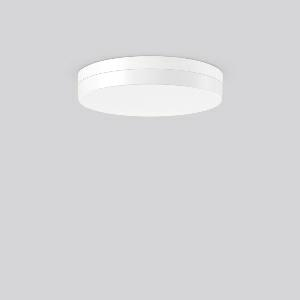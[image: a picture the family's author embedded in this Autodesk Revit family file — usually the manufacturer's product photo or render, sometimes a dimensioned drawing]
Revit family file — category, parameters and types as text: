
# Revit family: flat_slim_round_312631_002_19_3b17
name_source: partatom
category: Lighting Fixtures
units: mm (PartAtom-declared; Revit-internal decimal feet)

## family parameters
Cut with Voids When Loaded = No
Host = Face
Light Source = No
Part Type = Normal
Room Calculation Point = No
Round Connector Dimension = Use Diameter
Shared = No

## types (1)
- MultiLumen 1 830 (1 x LED Modul 830, 2450 lm, 3000)
    Apparent Load = 25 VA
    CIE Flux Codes = 40 70 90 84 100
    Color Rendering = 80
    Color Temperature = 3000
    Default Elevation = 1800 mm
    Height = 75 mm
    Lamp = 1 x LED Modul 830
    Lamp Light Flux = 2450 lm
    Lamp count = 1
    Length = 400 mm
    Lifetime = 50000 h
    Luminous efficacy = 98 lm/W
    Manufacturer = RZB
    ModVariant = No
    Model = 312631.002.19
    Mounting Place = Ceiling
    Mounting Type = Surface mounted
    Number of Poles = 1
    OnlyDefault = Yes
    Power Factor = 1
    Product Name = FLAT SLIM round
    Product group = Surface mounted ceiling and wall luminaires
    ProductGroupID = 305
    Protection Class = Protection class I
    Protection Degree = Degree of protection
    RLX_Detail_Level = 1
    RLX_Emergency_Light_Flux = 0 lm
    RLX_Emergency_Type = 0
    RLX_Emergency_Type_DB = No
    RlxData = <blob elided: 20513 chars, md5=5101872f>
    Socket = socket
    Standby Power = 0 W
    System Light Flux = 2450 lm
    System Power = 25 W
    Type Comments = MultiLumen 1 830
    Type Image = 312631.002.jpg
    URL = http://relux.com
    VarID = multilumen_1_830
    Voltage = 0 V
    Weight = 0.00 kg
    Width = 0 mm  [stored 0 ft]

note: [stored X ft] marks values corroborated as IEEE doubles in the binary element streams (Revit-internal decimal feet)

## geometry (parser evidence)
native form markers: Blend x4, Sweep x15
no freeform markers — native parametric forms only
